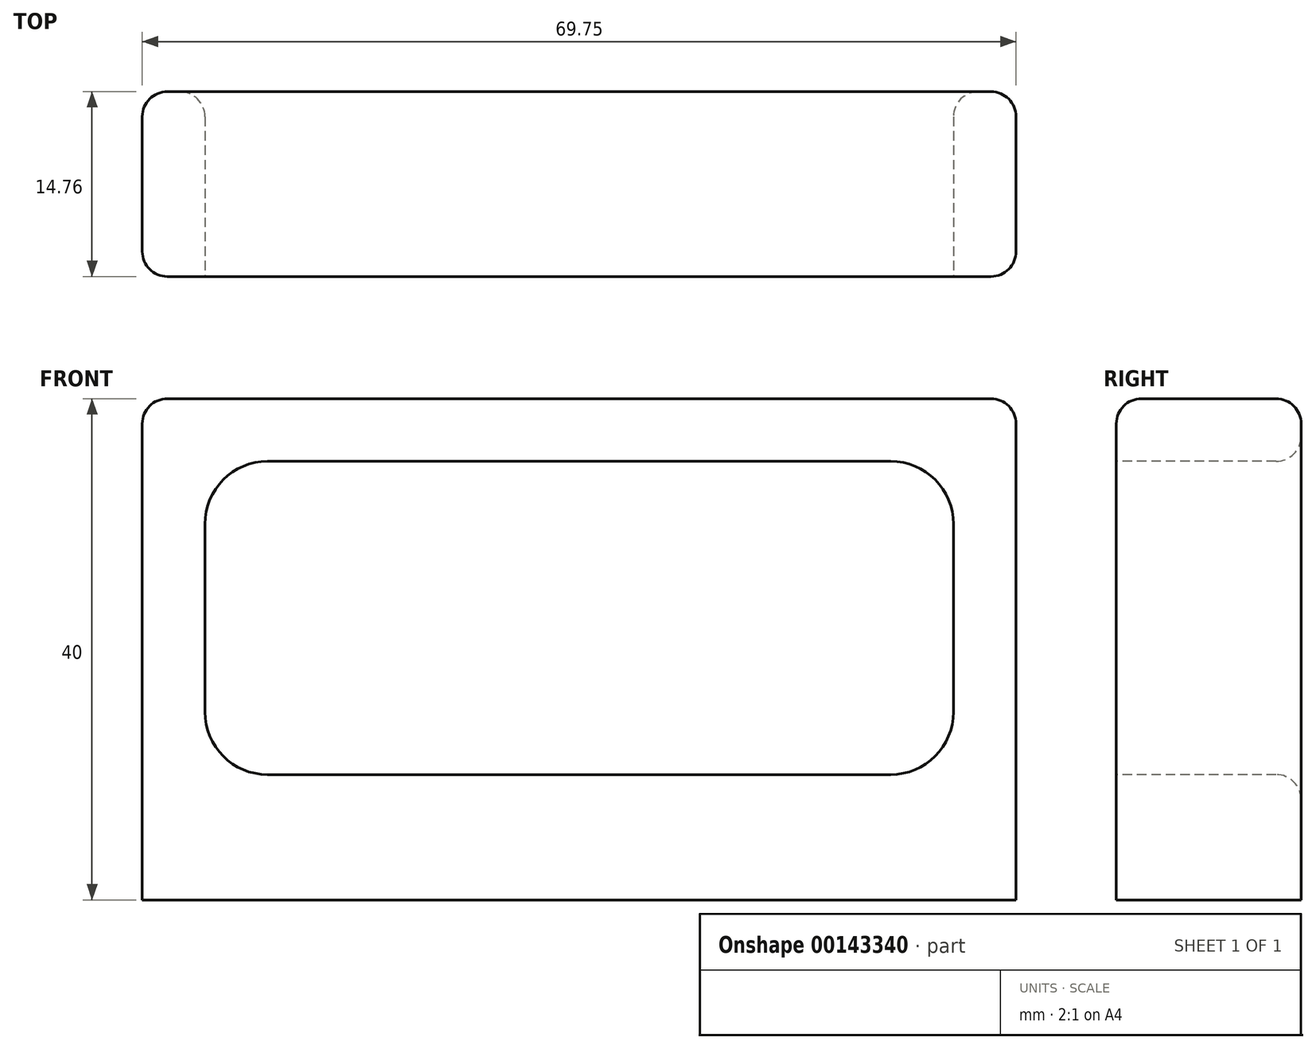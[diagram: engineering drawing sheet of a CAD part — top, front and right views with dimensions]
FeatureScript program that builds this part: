
annotation { "Feature Type Name" : "Feature", "Feature Type Description" : "" }
export const myFeature = defineFeature(function(context is Context, id is Id, definition is map)
    precondition{}
    {
        {
            var Q0;
            Q0=qCreatedBy(makeId("Top.planeOp"),FACE);
            var sketch = newSketch(context, id + "F0", { "sketchPlane" : qUnion([Q0])});
            skLineSegment(sketch, "E0.bottom", {"start": v(0, 7.38) * mm, "end": v(69.75, 7.38) * mm});
            skLineSegment(sketch, "E0.top", {"start": v(0, -7.38) * mm, "end": v(69.75, -7.38) * mm});
            skLineSegment(sketch, "E0.left", {"start": v(0, 7.38) * mm, "end": v(0, -7.38) * mm});
            skLineSegment(sketch, "E0.right", {"start": v(69.75, 7.38) * mm, "end": v(69.75, -7.38) * mm});
            skSolve(sketch);
        }
        {
            var Q0;
            Q0 = qSketchRegion(id + "F0", true);
            extrude(context, id + "F1", {"entities" : qUnion([Q0]), "depth" : 40 * mm});
        }
        {
            var Q0;
            Q0=makeQuery(id+"F1.opExtrude","CAP_EDGE",EDGE,{"disambiguationData":[OSD([sQuery(id+"F0.wireOp",EDGE,"E0.top")])],"isStart":false});
            var Q1;
            Q1=makeQuery(id+"F1.opExtrude","CAP_EDGE",EDGE,{"disambiguationData":[OSD([sQuery(id+"F0.wireOp",EDGE,"E0.bottom")])],"isStart":false});
            var Q2;
            Q2=makeQuery(id+"F1.opExtrude","CAP_EDGE",EDGE,{"disambiguationData":[OSD([sQuery(id+"F0.wireOp",EDGE,"E0.right")])],"isStart":false});
            var Q3;
            Q3=makeQuery(id+"F1.opExtrude","CAP_EDGE",EDGE,{"disambiguationData":[OSD([sQuery(id+"F0.wireOp",EDGE,"E0.left")])],"isStart":false});
            var Q4;
            Q4=makeQuery(id+"F1.opExtrude","SWEPT_EDGE",EDGE,{"disambiguationData":[OSD([sQuery(id+"F0.wireOp",EDGE,"E0.top"),sQuery(id+"F0.wireOp",EDGE,"E0.right")])]});
            var Q5;
            Q5=makeQuery(id+"F1.opExtrude","SWEPT_EDGE",EDGE,{"disambiguationData":[OSD([sQuery(id+"F0.wireOp",EDGE,"E0.bottom"),sQuery(id+"F0.wireOp",EDGE,"E0.right")])]});
            var Q6;
            Q6=makeQuery(id+"F1.opExtrude","SWEPT_EDGE",EDGE,{"disambiguationData":[OSD([sQuery(id+"F0.wireOp",EDGE,"E0.top"),sQuery(id+"F0.wireOp",EDGE,"E0.left")])]});
            var Q7;
            Q7=makeQuery(id+"F1.opExtrude","SWEPT_EDGE",EDGE,{"disambiguationData":[OSD([sQuery(id+"F0.wireOp",EDGE,"E0.bottom"),sQuery(id+"F0.wireOp",EDGE,"E0.left")])]});
            fillet(context, id + "F2", {"entities" : qUnion([Q0, Q1, Q2, Q3, Q4, Q5, Q6, Q7]), "radius" : 2 * mm, "tangentPropagation" : true, "allowEdgeOverflow" : false});
        }
        {
            var Q0;
            Q0=makeQuery(id+"F1.opExtrude","SWEPT_FACE",FACE,{"disambiguationData":[OSD([sQuery(id+"F0.wireOp",EDGE,"E0.top")])]});
            var sketch = newSketch(context, id + "F3", { "sketchPlane" : qUnion([Q0])});
            skLineSegment(sketch, "E1.bottom", {"start": v(10, 35) * mm, "end": v(59.75, 35) * mm});
            skLineSegment(sketch, "E1.top", {"start": v(10, 10) * mm, "end": v(59.75, 10) * mm});
            skLineSegment(sketch, "E1.left", {"start": v(5, 30) * mm, "end": v(5, 15) * mm});
            skLineSegment(sketch, "E1.right", {"start": v(64.75, 30) * mm, "end": v(64.75, 15) * mm});
            skPoint(sketch, "E2.visualSharp", {"position": v(5, 35) * mm});
            skArc(sketch, "E2.filletArc", {"start": v(10, 35) * mm, "mid": v(6.46, 33.54) * mm, "end": v(5, 30) * mm});
            skPoint(sketch, "E3.visualSharp", {"position": v(64.75, 35) * mm});
            skArc(sketch, "E3.filletArc", {"start": v(64.75, 30) * mm, "mid": v(63.29, 33.54) * mm, "end": v(59.75, 35) * mm});
            skPoint(sketch, "E4.visualSharp", {"position": v(64.75, 10) * mm});
            skArc(sketch, "E4.filletArc", {"start": v(59.75, 10) * mm, "mid": v(63.29, 11.46) * mm, "end": v(64.75, 15) * mm});
            skPoint(sketch, "E5.visualSharp", {"position": v(5, 10) * mm});
            skArc(sketch, "E5.filletArc", {"start": v(5, 15) * mm, "mid": v(6.46, 11.46) * mm, "end": v(10, 10) * mm});
            skSolve(sketch);
        }
        {
            var Q0;
            Q0 = qSketchRegion(id + "F3", true);
            extrude(context, id + "F4", {"entities" : qUnion([Q0]), "operationType" : NewBodyOperationType.REMOVE, "endBound" : BoundingType.THROUGH_ALL, "oppositeDirection" : true, "depth" : 25 * mm});
        }
        {
            var Q0;
            Q0=makeQuery(id+"F1.opExtrude","CAP_FACE",FACE,{"disambiguationData":[OSD([sQuery(id+"F0.wireOp",EDGE,"E0.bottom"),sQuery(id+"F0.wireOp",EDGE,"E0.top"),sQuery(id+"F0.wireOp",EDGE,"E0.left"),sQuery(id+"F0.wireOp",EDGE,"E0.right")])],"isStart":true});
            var sketch = newSketch(context, id + "F5", { "sketchPlane" : qUnion([Q0])});
            skLineSegment(sketch, "E6.0", {"start": v(2, 7.38) * mm, "end": v(67.75, 7.38) * mm});
            skArc(sketch, "E7.0", {"start": v(2, 7.38) * mm, "mid": v(0.59, 6.79) * mm, "end": v(0, 5.38) * mm});
            skLineSegment(sketch, "E8.0", {"start": v(0, -5.38) * mm, "end": v(0, 5.38) * mm});
            skArc(sketch, "E9.0", {"start": v(0, -5.38) * mm, "mid": v(0.59, -6.79) * mm, "end": v(2, -7.38) * mm});
            skLineSegment(sketch, "E10.0", {"start": v(2, -7.38) * mm, "end": v(67.75, -7.38) * mm});
            skArc(sketch, "E11.0", {"start": v(67.75, -7.38) * mm, "mid": v(69.16, -6.79) * mm, "end": v(69.75, -5.38) * mm});
            skLineSegment(sketch, "E12.0", {"start": v(69.75, -5.38) * mm, "end": v(69.75, 5.38) * mm});
            skArc(sketch, "E13.0", {"start": v(69.75, 5.38) * mm, "mid": v(69.16, 6.79) * mm, "end": v(67.75, 7.38) * mm});
            skSolve(sketch);
        }
        {
            var Q0;
            Q0=makeQuery(id+"F5.imprint","IMPRINT",FACE,{"disambiguationData":[TD([[makeQuery(id+"F5.imprint","IMPRINT",EDGE,{"derivedFrom":sQuery(id+"F5.wireOp",EDGE,"E6.0")}),-1.0]])]});
            var sketch = newSketch(context, id + "F6", { "sketchPlane" : qUnion([Q0])});
            skCircle(sketch, "E14", {"center": v(60.75, 0) * mm, "radius": 1.88 * mm});
            skCircle(sketch, "E15", {"center": v(44.75, 0) * mm, "radius": 1.88 * mm});
            skCircle(sketch, "E16", {"center": v(25, 0) * mm, "radius": 1.88 * mm});
            skCircle(sketch, "E17", {"center": v(9, 0) * mm, "radius": 1.88 * mm});
            skSolve(sketch);
        }
        {
            var Q0;
            Q0=makeQuery(id+"F4.boolean.opBoolean","COPY",EDGE,{"derivedFrom":makeQuery(id+"F4.opExtrude","CAP_EDGE",EDGE,{"disambiguationData":[OSD([sQuery(id+"F3.wireOp",EDGE,"E1.top")])],"isStart":true})});
            var Q1;
            Q1=makeQuery(id+"F4.boolean.opBoolean","INTERSECT",EDGE,{"derivedFrom":[makeQuery(id+"F1.opExtrude","SWEPT_FACE",FACE,{"disambiguationData":[OSD([sQuery(id+"F0.wireOp",EDGE,"E0.bottom")])]}),makeQuery(id+"F4.opExtrude","SWEPT_FACE",FACE,{"disambiguationData":[OSD([sQuery(id+"F3.wireOp",EDGE,"E1.top")])]})]});
            fillet(context, id + "F7", {"entities" : qUnion([Q0, Q1]), "radius" : 2 * mm, "tangentPropagation" : true, "allowEdgeOverflow" : false});
        }
    });
